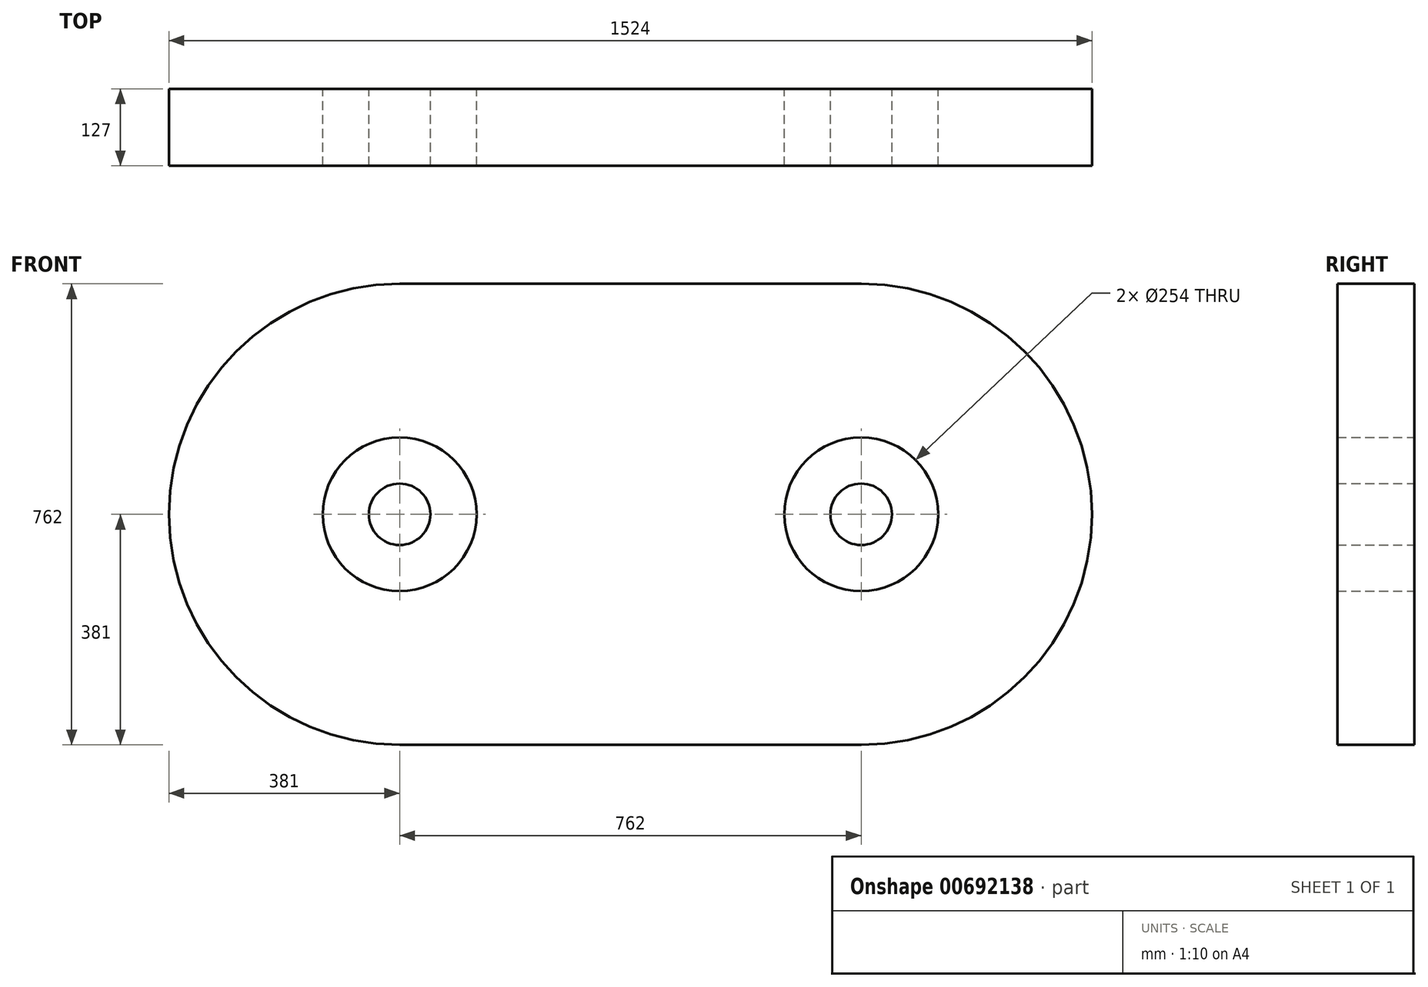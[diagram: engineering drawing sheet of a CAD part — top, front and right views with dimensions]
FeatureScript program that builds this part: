
annotation { "Feature Type Name" : "Feature", "Feature Type Description" : "" }
export const myFeature = defineFeature(function(context is Context, id is Id, definition is map)
    precondition{}
    {
        {
            var Q0;
            Q0=qCreatedBy(makeId("Front.planeOp"),FACE);
            var sketch = newSketch(context, id + "F0", { "sketchPlane" : qUnion([Q0])});
            skLineSegment(sketch, "E0.bottom", {"start": v(-381, 381) * mm, "end": v(381, 381) * mm});
            skLineSegment(sketch, "E0.top", {"start": v(-381, -381) * mm, "end": v(381, -381) * mm});
            skLineSegment(sketch, "E0.left", {"start": v(-381, 381) * mm, "end": v(-381, -381) * mm, "construction": true});
            skLineSegment(sketch, "E0.right", {"start": v(381, 381) * mm, "end": v(381, -381) * mm, "construction": true});
            skArc(sketch, "E1", {"start": v(-381, 381) * mm, "mid": v(-762, 0) * mm, "end": v(-381, -381) * mm});
            skArc(sketch, "E2.MirrorCS", {"start": v(381, 381) * mm, "mid": v(762, 0) * mm, "end": v(381, -381) * mm});
            skCircle(sketch, "E3", {"center": v(-381, 0) * mm, "radius": 127 * mm});
            skCircle(sketch, "E4", {"center": v(381, 0) * mm, "radius": 127 * mm});
            skCircle(sketch, "E5", {"center": v(-381, 0) * mm, "radius": 50.8 * mm});
            skCircle(sketch, "E6", {"center": v(381, 0) * mm, "radius": 50.8 * mm});
            skSolve(sketch);
        }
        {
            var Q0;
            Q0=qSketchRegion(id+"F0",true);
            var Q1;
            Q1=makeQuery(id+"F0.imprint","IMPRINT",FACE,{"disambiguationData":[TD([[makeQuery(id+"F0.imprint","IMPRINT",EDGE,{"derivedFrom":sQuery(id+"F0.wireOp",EDGE,"E5")}),1.0]])]});
            var Q2;
            Q2=makeQuery(id+"F0.imprint","IMPRINT",FACE,{"disambiguationData":[TD([[makeQuery(id+"F0.imprint","IMPRINT",EDGE,{"derivedFrom":sQuery(id+"F0.wireOp",EDGE,"E6")}),1.0]])]});
            extrude(context, id + "F1", {"entities" : qUnion([Q0, Q1, Q2]), "depth" : 127 * mm, "offsetDistance" : 25.4 * mm});
        }
    });
